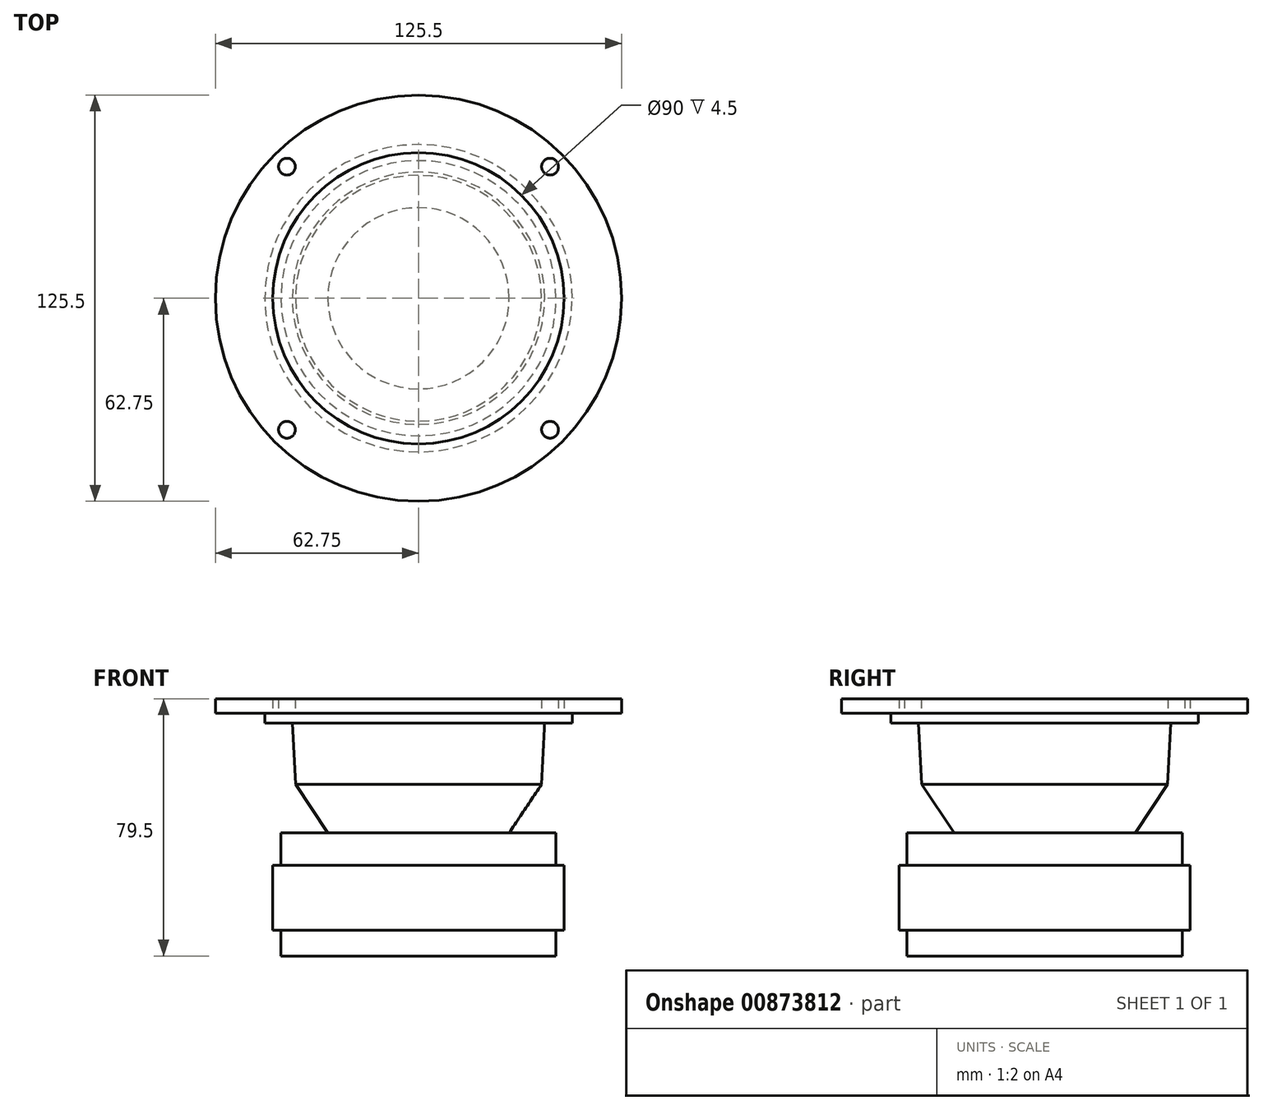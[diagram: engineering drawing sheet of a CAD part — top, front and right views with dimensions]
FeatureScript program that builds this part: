
annotation { "Feature Type Name" : "Feature", "Feature Type Description" : "" }
export const myFeature = defineFeature(function(context is Context, id is Id, definition is map)
    precondition{}
    {
        {
            var Q0;
            Q0=qCreatedBy(makeId("Right.planeOp"),FACE);
            var sketch = newSketch(context, id + "F0", { "sketchPlane" : qUnion([Q0])});
            skLineSegment(sketch, "E0.bottom", {"start": v(0, 0) * mm, "end": v(-62.75, 0) * mm});
            skLineSegment(sketch, "E0.top", {"start": v(0, 4.2) * mm, "end": v(-62.75, 4.2) * mm});
            skLineSegment(sketch, "E0.left", {"start": v(62.75, 0) * mm, "end": v(62.75, 4.2) * mm});
            skLineSegment(sketch, "E0.right", {"start": v(-62.75, 0) * mm, "end": v(-62.75, 4.2) * mm});
            skPoint(sketch, "E0.middle", {"position": v(0, 2.1) * mm});
            skLineSegment(sketch, "E1.bottom", {"start": v(-45, -47) * mm, "end": v(0, -47) * mm});
            skLineSegment(sketch, "E1.top", {"start": v(-45, -67) * mm, "end": v(0, -67) * mm});
            skLineSegment(sketch, "E1.left", {"start": v(-45, -47) * mm, "end": v(-45, -67) * mm});
            skPoint(sketch, "E1.middle", {"position": v(0, -57) * mm});
            skLineSegment(sketch, "E2.bottom", {"start": v(-42.5, -47) * mm, "end": v(0, -47) * mm});
            skLineSegment(sketch, "E2.top", {"start": v(-42.5, -37) * mm, "end": v(0, -37) * mm});
            skLineSegment(sketch, "E2.left", {"start": v(-42.5, -47) * mm, "end": v(-42.5, -37) * mm});
            skPoint(sketch, "E2.middle", {"position": v(0, -42) * mm});
            skLineSegment(sketch, "E3", {"start": v(-28, -37) * mm, "end": v(-38, -22) * mm});
            skLineSegment(sketch, "E4", {"start": v(-38, -22) * mm, "end": v(-39, -3) * mm});
            skLineSegment(sketch, "E5", {"start": v(-39, -3) * mm, "end": v(-47.5, -3) * mm});
            skLineSegment(sketch, "E6", {"start": v(-47.5, -3) * mm, "end": v(-47.5, 0) * mm});
            skLineSegment(sketch, "E7", {"start": v(0, 61.03) * mm, "end": v(0, -138.38) * mm, "construction": true});
            skLineSegment(sketch, "E8.bottom", {"start": v(-42.5, -67) * mm, "end": v(0, -67) * mm});
            skLineSegment(sketch, "E8.top", {"start": v(-42.5, -75) * mm, "end": v(0, -75) * mm});
            skLineSegment(sketch, "E8.left", {"start": v(-42.5, -67) * mm, "end": v(-42.5, -75) * mm});
            skPoint(sketch, "E8.middle", {"position": v(0, -71) * mm});
            skLineSegment(sketch, "E9", {"start": v(0, 0) * mm, "end": v(0, -75) * mm});
            skSolve(sketch);
        }
        {
            var Q0;
            Q0=qCreatedBy(makeId("Top.planeOp"),FACE);
            var sketch = newSketch(context, id + "F1", { "sketchPlane" : qUnion([Q0])});
            skCircle(sketch, "E10", {"center": v(0, 0) * mm, "radius": 57.5 * mm, "construction": true});
            skLineSegment(sketch, "E11", {"start": v(0, 0) * mm, "end": v(-40.66, -40.66) * mm, "construction": true});
            skCircle(sketch, "E12", {"center": v(-40.66, -40.66) * mm, "radius": 2.6 * mm});
            skLineSegment(sketch, "E13", {"start": v(-66.8, 0) * mm, "end": v(71.94, 0) * mm, "construction": true});
            skLineSegment(sketch, "E14", {"start": v(0, -68.55) * mm, "end": v(0, 71.6) * mm, "construction": true});
            skCircle(sketch, "E15.MirrorC", {"center": v(-40.66, 40.66) * mm, "radius": 2.6 * mm});
            skCircle(sketch, "E16.MirrorC", {"center": v(40.66, -40.66) * mm, "radius": 2.6 * mm});
            skCircle(sketch, "E17.MirrorC", {"center": v(40.66, 40.66) * mm, "radius": 2.6 * mm});
            skCircle(sketch, "E18", {"center": v(0, 0) * mm, "radius": 62.75 * mm});
            skPoint(sketch, "E19", {"position": v(0, -62.75) * mm});
            skCircle(sketch, "E20", {"center": v(0, 0) * mm, "radius": 45 * mm});
            skSolve(sketch);
        }
        {
            var Q0;
            Q0=qSketchRegion(id+"F0",true);
            var Q1;
            Q1=qConstructionFilter(qBodyType(qCreatedBy(id+"F0",EDGE),BodyType.WIRE),ConstructionObject.NO);
            var Q2;
            Q2=sQuery(id+"F0.wireOp",EDGE,"E7");
            revolve(context, id + "F2", {"surfaceOperationType" : NewSurfaceOperationType.NEW, "entities" : qUnion([Q0]), "surfaceEntities" : qUnion([Q1]), "axis" : qUnion([Q2]), "revolveType" : RevolveType.FULL});
        }
        {
            var Q0;
            Q0=qSketchRegion(id+"F1",true);
            extrude(context, id + "F3", {"entities" : qUnion([Q0]), "operationType" : NewBodyOperationType.ADD, "depth" : 4.5 * mm, "offsetDistance" : 25 * mm});
        }
    });
